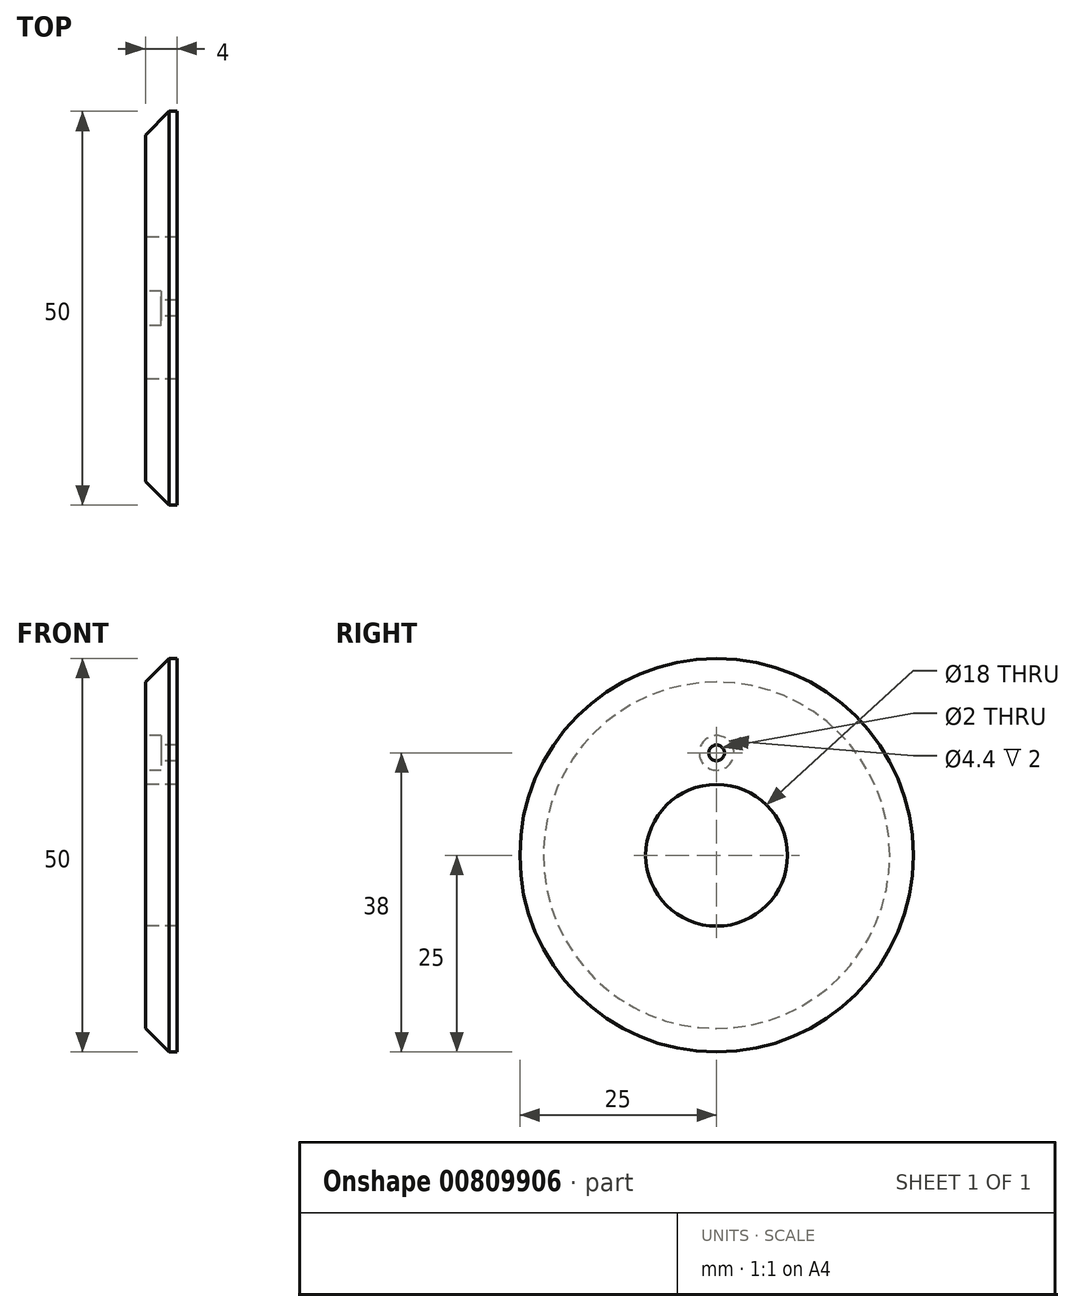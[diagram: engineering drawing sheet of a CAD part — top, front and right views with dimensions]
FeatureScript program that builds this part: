
annotation { "Feature Type Name" : "Feature", "Feature Type Description" : "" }
export const myFeature = defineFeature(function(context is Context, id is Id, definition is map)
    precondition{}
    {
        {
            var Q0;
            Q0=qCreatedBy(makeId("Front.planeOp"),FACE);
            var sketch = newSketch(context, id + "F0", { "sketchPlane" : qUnion([Q0])});
            skLineSegment(sketch, "E0", {"start": v(0, 9) * mm, "end": v(0, 25) * mm});
            skLineSegment(sketch, "E1", {"start": v(0, 25) * mm, "end": v(-1, 25) * mm});
            skLineSegment(sketch, "E2", {"start": v(-1, 25) * mm, "end": v(-4, 22) * mm});
            skLineSegment(sketch, "E3", {"start": v(-4, 22) * mm, "end": v(-4, 9) * mm});
            skLineSegment(sketch, "E4", {"start": v(-4, 0) * mm, "end": v(0, 0) * mm});
            skLineSegment(sketch, "E5", {"start": v(0, 9) * mm, "end": v(-4, 9) * mm});
            skSolve(sketch);
        }
        {
            var Q0;
            Q0 = qSketchRegion(id + "F0", true);
            var Q1;
            Q1=sQuery(id+"F0.wireOp",EDGE,"E4");
            revolve(context, id + "F1", {"surfaceOperationType" : NewSurfaceOperationType.NEW, "entities" : qUnion([Q0]), "axis" : qUnion([Q1]), "revolveType" : RevolveType.FULL});
        }
        {
            var Q0;
            Q0=makeQuery(id+"F1.opRevolve","SWEPT_FACE",FACE,{"disambiguationData":[OSD([sQuery(id+"F0.wireOp",EDGE,"E3")])]});
            var sketch = newSketch(context, id + "F2", { "sketchPlane" : qUnion([Q0])});
            skCircle(sketch, "E6", {"center": v(0, 0) * mm, "radius": 13 * mm});
            skPoint(sketch, "E7", {"position": v(0, 13) * mm});
            skSolve(sketch);
        }
        {
            var Q0;
            Q0=sQuery(id+"F2.wireOp",VERTEX,"E7");
            var Q1;
            Q1=makeQuery(id+"F1.opRevolve","SWEPT_BODY",BODY,{"disambiguationData":[OSD([sQuery(id+"F0.wireOp",EDGE,"E0"),sQuery(id+"F0.wireOp",EDGE,"E1"),sQuery(id+"F0.wireOp",EDGE,"E2"),sQuery(id+"F0.wireOp",EDGE,"E3"),sQuery(id+"F0.wireOp",EDGE,"E5")])]});
            hole(context, id + "F3", {"style" : HoleStyle.C_BORE, "endStyle" : HoleEndStyle.BLIND, "holeDiameter" : 2 * mm, "cBoreDiameter" : 4.4 * mm, "cBoreDepth" : 2 * mm, "majorDiameter" : 5 * mm, "holeDepth" : 4 * mm, "isTappedThrough" : true, "tappedDepth" : 12 * mm, "tapClearance" : 3, "startFromSketch" : true, "locations" : qUnion([Q0]), "scope" : qUnion([Q1])});
        }
    });
